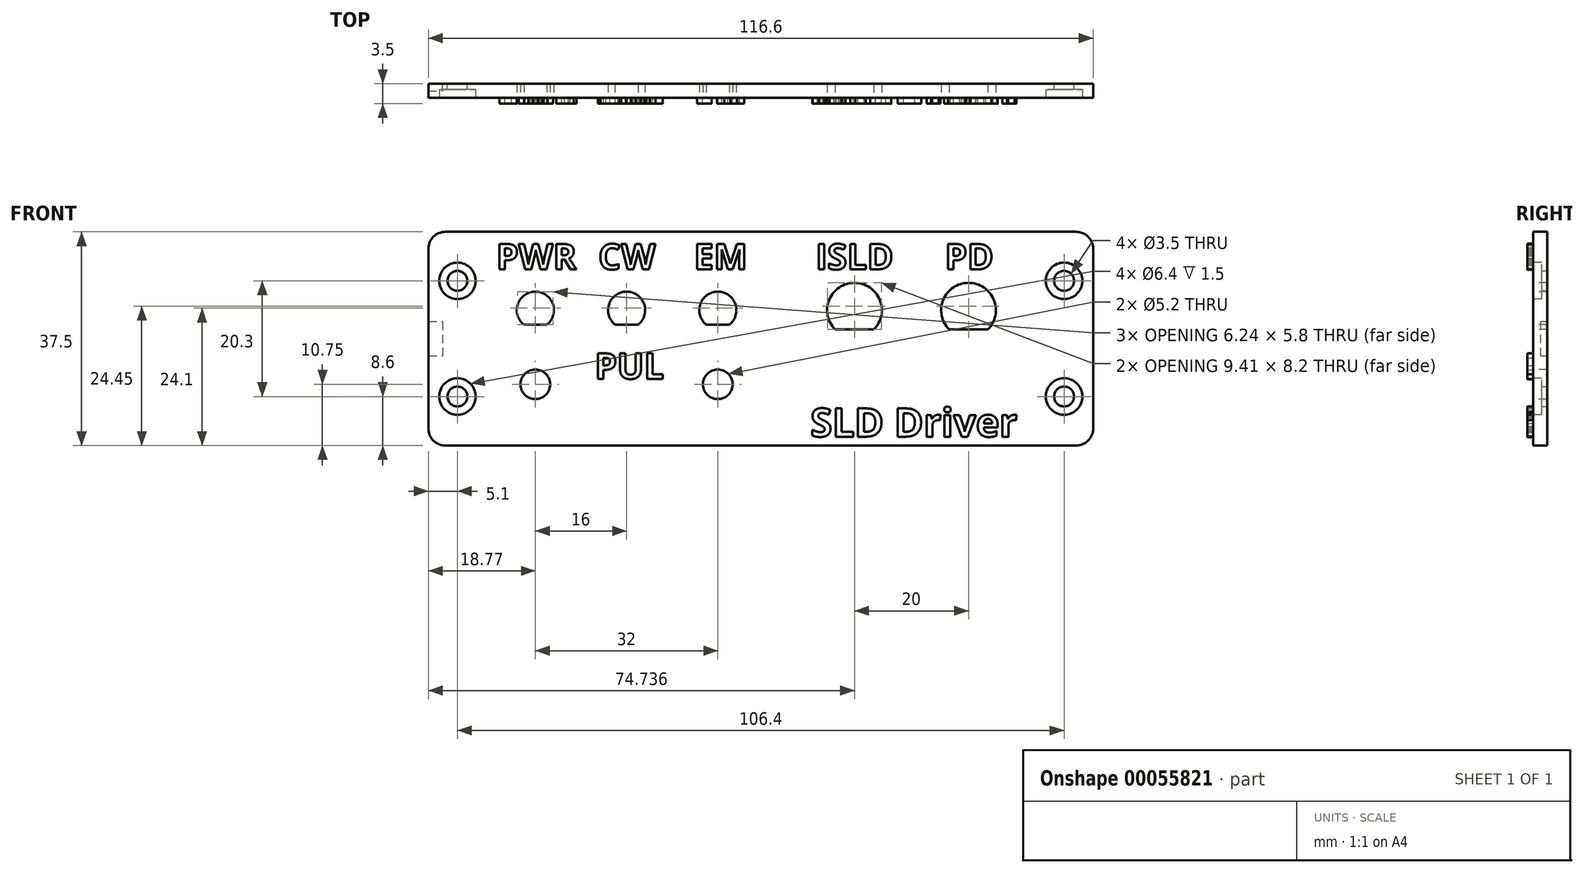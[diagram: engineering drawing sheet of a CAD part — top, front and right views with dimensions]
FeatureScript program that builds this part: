
annotation { "Feature Type Name" : "Feature", "Feature Type Description" : "" }
export const myFeature = defineFeature(function(context is Context, id is Id, definition is map)
    precondition{}
    {
        {
            var Q0;
            Q0=qCreatedBy(makeId("Front.planeOp"),FACE);
            var sketch = newSketch(context, id + "F0", { "sketchPlane" : qUnion([Q0])});
            skLineSegment(sketch, "E0.bottom", {"start": v(-55.3, 18.75) * mm, "end": v(55.3, 18.75) * mm});
            skLineSegment(sketch, "E0.top", {"start": v(-55.3, -18.75) * mm, "end": v(55.3, -18.75) * mm});
            skLineSegment(sketch, "E0.left", {"start": v(-58.3, 15.75) * mm, "end": v(-58.3, -15.75) * mm});
            skLineSegment(sketch, "E0.right", {"start": v(58.3, 15.75) * mm, "end": v(58.3, -15.75) * mm});
            skPoint(sketch, "E1.visualSharp", {"position": v(-58.3, 18.75) * mm});
            skArc(sketch, "E1.filletArc", {"start": v(-55.3, 18.75) * mm, "mid": v(-57.42, 17.87) * mm, "end": v(-58.3, 15.75) * mm});
            skPoint(sketch, "E2.visualSharp", {"position": v(58.3, 18.75) * mm});
            skArc(sketch, "E2.filletArc", {"start": v(58.3, 15.75) * mm, "mid": v(57.42, 17.87) * mm, "end": v(55.3, 18.75) * mm});
            skPoint(sketch, "E3.visualSharp", {"position": v(58.3, -18.75) * mm});
            skArc(sketch, "E3.filletArc", {"start": v(55.3, -18.75) * mm, "mid": v(57.42, -17.87) * mm, "end": v(58.3, -15.75) * mm});
            skPoint(sketch, "E4.visualSharp", {"position": v(-58.3, -18.75) * mm});
            skArc(sketch, "E4.filletArc", {"start": v(-58.3, -15.75) * mm, "mid": v(-57.42, -17.87) * mm, "end": v(-55.3, -18.75) * mm});
            skCircle(sketch, "E5", {"center": v(-53.2, 10.15) * mm, "radius": 1.75 * mm});
            skCircle(sketch, "E6", {"center": v(53.2, 10.15) * mm, "radius": 1.75 * mm});
            skCircle(sketch, "E7", {"center": v(-53.2, -10.15) * mm, "radius": 1.75 * mm});
            skCircle(sketch, "E8", {"center": v(53.2, -10.15) * mm, "radius": 1.75 * mm});
            skSolve(sketch);
        }
        {
            var Q0;
            Q0=makeQuery(id+"F0.imprint","IMPRINT",FACE,{"disambiguationData":[TD([[makeQuery(id+"F0.imprint","IMPRINT",EDGE,{"derivedFrom":sQuery(id+"F0.wireOp",EDGE,"E0.bottom")}),-1.0]])]});
            extrude(context, id + "F1", {"entities" : qUnion([Q0]), "depth" : 2.5 * mm});
        }
        {
            var Q0;
            Q0=makeQuery(id+"F1.opExtrude","CAP_FACE",FACE,{"disambiguationData":[OSD([sQuery(id+"F0.wireOp",EDGE,"E0.bottom"),sQuery(id+"F0.wireOp",EDGE,"E0.top"),sQuery(id+"F0.wireOp",EDGE,"E0.left"),sQuery(id+"F0.wireOp",EDGE,"E0.right"),sQuery(id+"F0.wireOp",EDGE,"E1.filletArc"),sQuery(id+"F0.wireOp",EDGE,"E2.filletArc"),sQuery(id+"F0.wireOp",EDGE,"E3.filletArc"),sQuery(id+"F0.wireOp",EDGE,"E4.filletArc"),sQuery(id+"F0.wireOp",EDGE,"E5"),sQuery(id+"F0.wireOp",EDGE,"E6"),sQuery(id+"F0.wireOp",EDGE,"E7"),sQuery(id+"F0.wireOp",EDGE,"E8")])],"isStart":false});
            var sketch = newSketch(context, id + "F2", { "sketchPlane" : qUnion([Q0])});
            skCircle(sketch, "E9", {"center": v(-53.2, 10.15) * mm, "radius": 3.2 * mm});
            skCircle(sketch, "E10", {"center": v(53.2, 10.15) * mm, "radius": 3.2 * mm});
            skCircle(sketch, "E11", {"center": v(-53.2, -10.15) * mm, "radius": 3.2 * mm});
            skCircle(sketch, "E12", {"center": v(53.2, -10.15) * mm, "radius": 3.2 * mm});
            skSolve(sketch);
        }
        {
            var Q0;
            Q0 = qSketchRegion(id + "F2", true);
            extrude(context, id + "F3", {"entities" : qUnion([Q0]), "operationType" : NewBodyOperationType.REMOVE, "oppositeDirection" : true, "depth" : 1.5 * mm});
        }
        {
            var Q0;
            Q0=makeQuery(id+"F1.opExtrude","CAP_FACE",FACE,{"disambiguationData":[OSD([sQuery(id+"F0.wireOp",EDGE,"E0.bottom"),sQuery(id+"F0.wireOp",EDGE,"E0.top"),sQuery(id+"F0.wireOp",EDGE,"E0.left"),sQuery(id+"F0.wireOp",EDGE,"E0.right"),sQuery(id+"F0.wireOp",EDGE,"E1.filletArc"),sQuery(id+"F0.wireOp",EDGE,"E2.filletArc"),sQuery(id+"F0.wireOp",EDGE,"E3.filletArc"),sQuery(id+"F0.wireOp",EDGE,"E4.filletArc"),sQuery(id+"F0.wireOp",EDGE,"E5"),sQuery(id+"F0.wireOp",EDGE,"E6"),sQuery(id+"F0.wireOp",EDGE,"E7"),sQuery(id+"F0.wireOp",EDGE,"E8")])],"isStart":true});
            var sketch = newSketch(context, id + "F4", { "sketchPlane" : qUnion([Q0])});
            skLineSegment(sketch, "E13.bottom", {"start": v(58.3, 3) * mm, "end": v(55.8, 3) * mm});
            skLineSegment(sketch, "E13.top", {"start": v(58.3, -3) * mm, "end": v(55.8, -3) * mm});
            skLineSegment(sketch, "E13.left", {"start": v(58.3, 3) * mm, "end": v(58.3, -3) * mm});
            skLineSegment(sketch, "E13.right", {"start": v(55.8, 3) * mm, "end": v(55.8, -3) * mm});
            skSolve(sketch);
        }
        {
            var Q0;
            Q0 = qSketchRegion(id + "F4", true);
            extrude(context, id + "F5", {"entities" : qUnion([Q0]), "operationType" : NewBodyOperationType.REMOVE, "oppositeDirection" : true, "depth" : 1.25 * mm});
        }
        {
            var Q0;
            Q0=makeQuery(id+"F1.opExtrude","CAP_FACE",FACE,{"disambiguationData":[OSD([sQuery(id+"F0.wireOp",EDGE,"E0.bottom"),sQuery(id+"F0.wireOp",EDGE,"E0.top"),sQuery(id+"F0.wireOp",EDGE,"E0.left"),sQuery(id+"F0.wireOp",EDGE,"E0.right"),sQuery(id+"F0.wireOp",EDGE,"E1.filletArc"),sQuery(id+"F0.wireOp",EDGE,"E2.filletArc"),sQuery(id+"F0.wireOp",EDGE,"E3.filletArc"),sQuery(id+"F0.wireOp",EDGE,"E4.filletArc"),sQuery(id+"F0.wireOp",EDGE,"E5"),sQuery(id+"F0.wireOp",EDGE,"E6"),sQuery(id+"F0.wireOp",EDGE,"E7"),sQuery(id+"F0.wireOp",EDGE,"E8")])],"isStart":false});
            var sketch = newSketch(context, id + "F6", { "sketchPlane" : qUnion([Q0])});
            skLineSegment(sketch, "E14", {"start": v(-63.46, 5) * mm, "end": v(64.15, 5) * mm, "construction": true});
            skArc(sketch, "E15", {"start": v(-37.52, 2.45) * mm, "mid": v(-39.53, 8.25) * mm, "end": v(-41.55, 2.45) * mm});
            skArc(sketch, "E16", {"start": v(-21.52, 2.45) * mm, "mid": v(-23.53, 8.25) * mm, "end": v(-25.55, 2.45) * mm});
            skArc(sketch, "E17", {"start": v(-5.52, 2.45) * mm, "mid": v(-7.53, 8.25) * mm, "end": v(-9.55, 2.45) * mm});
            skArc(sketch, "E18", {"start": v(39.82, 1.6) * mm, "mid": v(36.44, 9.8) * mm, "end": v(33.05, 1.6) * mm});
            skArc(sketch, "E19", {"start": v(19.82, 1.6) * mm, "mid": v(16.44, 9.8) * mm, "end": v(13.05, 1.6) * mm});
            skLineSegment(sketch, "E20", {"start": v(-48.3, 18.75) * mm, "end": v(-48.3, -12.75) * mm, "construction": true});
            skLineSegment(sketch, "E21", {"start": v(-48.3, -12.75) * mm, "end": v(48.3, -12.75) * mm, "construction": true});
            skLineSegment(sketch, "E22", {"start": v(48.3, -12.75) * mm, "end": v(48.3, 18.75) * mm, "construction": true});
            skLineSegment(sketch, "E23", {"start": v(-41.55, 2.45) * mm, "end": v(-37.52, 2.45) * mm});
            skLineSegment(sketch, "E24.trimOffspring", {"start": v(-25.55, 2.45) * mm, "end": v(-21.52, 2.45) * mm});
            skLineSegment(sketch, "E25.trimOffspring", {"start": v(-9.55, 2.45) * mm, "end": v(-5.52, 2.45) * mm});
            skLineSegment(sketch, "E26", {"start": v(13.05, 1.6) * mm, "end": v(19.82, 1.6) * mm});
            skLineSegment(sketch, "E27.trimOffspring", {"start": v(33.05, 1.6) * mm, "end": v(39.82, 1.6) * mm});
            skLineSegment(sketch, "E28", {"start": v(11.1, 9.8) * mm, "end": v(46.97, 9.8) * mm, "construction": true});
            skLineSegment(sketch, "E29", {"start": v(-42.3, 8.25) * mm, "end": v(6.57, 8.25) * mm, "construction": true});
            skCircle(sketch, "E30", {"center": v(-39.53, -8) * mm, "radius": 2.6 * mm});
            skCircle(sketch, "E31", {"center": v(-7.53, -8) * mm, "radius": 2.6 * mm});
            skLineSegment(sketch, "E32", {"start": v(-63, -8) * mm, "end": v(6.15, -8) * mm, "construction": true});
            skSolve(sketch);
        }
        {
            var Q0;
            Q0 = qSketchRegion(id + "F6", true);
            extrude(context, id + "F7", {"entities" : qUnion([Q0]), "operationType" : NewBodyOperationType.REMOVE, "endBound" : BoundingType.THROUGH_ALL, "oppositeDirection" : true, "depth" : 25 * mm});
        }
        {
            var Q0;
            Q0=makeQuery(id+"F1.opExtrude","CAP_FACE",FACE,{"disambiguationData":[OSD([sQuery(id+"F0.wireOp",EDGE,"E0.bottom"),sQuery(id+"F0.wireOp",EDGE,"E0.top"),sQuery(id+"F0.wireOp",EDGE,"E0.left"),sQuery(id+"F0.wireOp",EDGE,"E0.right"),sQuery(id+"F0.wireOp",EDGE,"E1.filletArc"),sQuery(id+"F0.wireOp",EDGE,"E2.filletArc"),sQuery(id+"F0.wireOp",EDGE,"E3.filletArc"),sQuery(id+"F0.wireOp",EDGE,"E4.filletArc"),sQuery(id+"F0.wireOp",EDGE,"E5"),sQuery(id+"F0.wireOp",EDGE,"E6"),sQuery(id+"F0.wireOp",EDGE,"E7"),sQuery(id+"F0.wireOp",EDGE,"E8")])],"isStart":false});
            var sketch = newSketch(context, id + "F8", { "sketchPlane" : qUnion([Q0])});
            skText(sketch, "E33", { "text": "PWR", "fontName": "OpenSans-Bold.ttf"});
            skLineSegment(sketch, "E34", {"start": v(-84.62, 12.15) * mm, "end": v(84.91, 12.15) * mm, "construction": true});
            skText(sketch, "E35", { "text": "CW", "fontName": "OpenSans-Bold.ttf"});
            skText(sketch, "E36", { "text": "EM", "fontName": "OpenSans-Bold.ttf"});
            skText(sketch, "E37", { "text": "ISLD", "fontName": "OpenSans-Bold.ttf"});
            skText(sketch, "E38", { "text": "PD", "fontName": "OpenSans-Bold.ttf"});
            const initialGuessF8  = {"E33": [-0.0464, 0.01215, 1, 0, 0.0045], "E35": [-0.0285, 0.01215, 1, 0, 0.0045], "E36": [-0.01172, 0.01215, 1, 0, 0.0045], "E37": [0.0096, 0.01215, 1, 0, 0.0045], "E38": [0.03227, 0.01215, 1, 0, 0.0045]};
            skSetInitialGuess(sketch, initialGuessF8);
            skSolve(sketch);
        }
        {
            var Q0;
            Q0 = qSketchRegion(id + "F8", true);
            extrude(context, id + "F9", {"entities" : qUnion([Q0]), "operationType" : NewBodyOperationType.ADD, "depth" : 1 * mm});
        }
        {
            var Q0;
            {var subQ0=sQuery(id+"F0.wireOp",EDGE,"E0.right");var subQ1=sQuery(id+"F0.wireOp",EDGE,"E3.filletArc");var subQ2=sQuery(id+"F0.wireOp",EDGE,"E4.filletArc");var subQ3=sQuery(id+"F0.wireOp",EDGE,"E1.filletArc");var subQ4=sQuery(id+"F0.wireOp",EDGE,"E0.top");var subQ5=sQuery(id+"F0.wireOp",EDGE,"E0.left");var subQ6=sQuery(id+"F0.wireOp",EDGE,"E2.filletArc");var subQ7=sQuery(id+"F0.wireOp",EDGE,"E0.bottom");Q0=makeQuery(id+"F9.boolean.opBoolean","SPLIT",FACE,{"disambiguationData":[TD([makeQuery(id+"F1.opExtrude","SWEPT_FACE",FACE,{"disambiguationData":[OSD([subQ7])]})])],"derivedFrom":makeQuery(id+"F1.opExtrude","CAP_FACE",FACE,{"disambiguationData":[OSD([subQ7,subQ4,subQ5,subQ0,subQ3,subQ6,subQ1,subQ2,sQuery(id+"F0.wireOp",EDGE,"E5"),sQuery(id+"F0.wireOp",EDGE,"E6"),sQuery(id+"F0.wireOp",EDGE,"E7"),sQuery(id+"F0.wireOp",EDGE,"E8")])],"isStart":false})});}
            var sketch = newSketch(context, id + "F10", { "sketchPlane" : qUnion([Q0])});
            skText(sketch, "E39", { "text": "PUL", "fontName": "OpenSans-Bold.ttf"});
            const initialGuessF10  = {"E39": [-0.02913, -0.00705, 1, 0, 0.0045]};
            skSetInitialGuess(sketch, initialGuessF10);
            skSolve(sketch);
        }
        {
            var Q0;
            Q0 = qSketchRegion(id + "F10", true);
            extrude(context, id + "F11", {"entities" : qUnion([Q0]), "operationType" : NewBodyOperationType.ADD, "depth" : 1 * mm});
        }
        {
            var Q0;
            {var subQ70=sQuery(id+"F0.wireOp",EDGE,"E0.right");var subQ114=sQuery(id+"F0.wireOp",EDGE,"E3.filletArc");var subQ120=sQuery(id+"F0.wireOp",EDGE,"E4.filletArc");var subQ132=sQuery(id+"F0.wireOp",EDGE,"E1.filletArc");var subQ140=sQuery(id+"F0.wireOp",EDGE,"E0.top");var subQ143=sQuery(id+"F0.wireOp",EDGE,"E0.left");var subQ152=sQuery(id+"F0.wireOp",EDGE,"E2.filletArc");var subQ182=sQuery(id+"F0.wireOp",EDGE,"E0.bottom");var subQ183=makeQuery(id+"F1.opExtrude","SWEPT_FACE",FACE,{"disambiguationData":[OSD([subQ182])]});Q0=makeQuery(id+"F11.boolean.opBoolean","SPLIT",FACE,{"disambiguationData":[TD([subQ183])],"derivedFrom":makeQuery(id+"F9.boolean.opBoolean","SPLIT",FACE,{"disambiguationData":[TD([subQ183])],"derivedFrom":makeQuery(id+"F1.opExtrude","CAP_FACE",FACE,{"disambiguationData":[OSD([subQ182,subQ140,subQ143,subQ70,subQ132,subQ152,subQ114,subQ120,sQuery(id+"F0.wireOp",EDGE,"E5"),sQuery(id+"F0.wireOp",EDGE,"E6"),sQuery(id+"F0.wireOp",EDGE,"E7"),sQuery(id+"F0.wireOp",EDGE,"E8")])],"isStart":false})})});}
            var sketch = newSketch(context, id + "F12", { "sketchPlane" : qUnion([Q0])});
            skText(sketch, "E40", { "text": "SLD Driver", "fontName": "OpenSans-Bold.ttf"});
            const initialGuessF12  = {"E40": [0.00869, -0.0172, 1, 0, 0.005]};
            skSetInitialGuess(sketch, initialGuessF12);
            skSolve(sketch);
        }
        {
            var Q0;
            Q0 = qSketchRegion(id + "F12", true);
            extrude(context, id + "F13", {"entities" : qUnion([Q0]), "operationType" : NewBodyOperationType.ADD, "depth" : 1 * mm});
        }
    });
